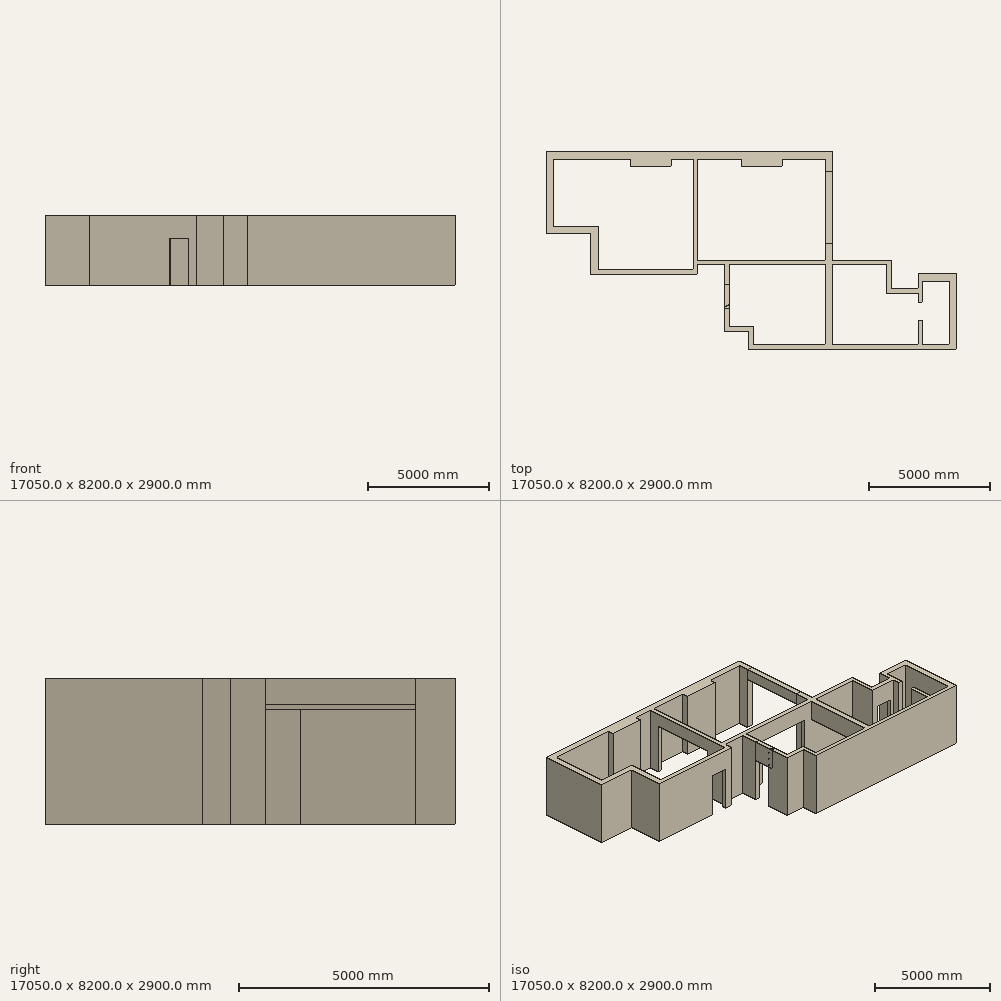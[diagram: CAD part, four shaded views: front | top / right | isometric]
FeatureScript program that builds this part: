
annotation { "Feature Type Name" : "Feature", "Feature Type Description" : "" }
export const myFeature = defineFeature(function(context is Context, id is Id, definition is map)
    precondition{}
    {
        {
            var Q0;
            Q0=qCreatedBy(makeId("Top.planeOp"),FACE);
            var sketch = newSketch(context, id + "F0", { "sketchPlane" : qUnion([Q0])});
            skLineSegment(sketch, "E0", {"start": v(-8264.98, 3800) * mm, "end": v(3635.02, 3800) * mm});
            skLineSegment(sketch, "E1", {"start": v(3635.02, 3800) * mm, "end": v(3635.02, 3000) * mm});
            skLineSegment(sketch, "E2", {"start": v(3635.02, 3000) * mm, "end": v(3335.02, 3000) * mm});
            skLineSegment(sketch, "E3", {"start": v(3335.02, 3000) * mm, "end": v(3335.02, 3500) * mm});
            skLineSegment(sketch, "E4", {"start": v(3335.02, 3500) * mm, "end": v(1535.02, 3500) * mm});
            skLineSegment(sketch, "E5", {"start": v(1535.02, 3500) * mm, "end": v(1535.02, 3200) * mm});
            skLineSegment(sketch, "E6", {"start": v(1535.02, 3200) * mm, "end": v(-164.98, 3200) * mm});
            skLineSegment(sketch, "E7", {"start": v(-164.98, 3200) * mm, "end": v(-164.98, 3500) * mm});
            skLineSegment(sketch, "E8", {"start": v(-164.98, 3500) * mm, "end": v(-1964.98, 3500) * mm});
            skLineSegment(sketch, "E9", {"start": v(-1964.98, 3500) * mm, "end": v(-1964.98, 3000) * mm});
            skLineSegment(sketch, "E10", {"start": v(-1964.98, 3000) * mm, "end": v(-2164.98, 3000) * mm});
            skLineSegment(sketch, "E11", {"start": v(-2164.98, 3000) * mm, "end": v(-2164.98, 3500) * mm});
            skLineSegment(sketch, "E12", {"start": v(-2164.98, 3500) * mm, "end": v(-3064.98, 3500) * mm});
            skLineSegment(sketch, "E13", {"start": v(-3064.98, 3500) * mm, "end": v(-3064.98, 3200) * mm});
            skLineSegment(sketch, "E14", {"start": v(-3064.98, 3200) * mm, "end": v(-4764.98, 3200) * mm});
            skLineSegment(sketch, "E15", {"start": v(-4764.98, 3200) * mm, "end": v(-4764.98, 3500) * mm});
            skLineSegment(sketch, "E16", {"start": v(-4764.98, 3500) * mm, "end": v(-7964.98, 3500) * mm});
            skLineSegment(sketch, "E17", {"start": v(-7964.98, 3500) * mm, "end": v(-7964.98, 700) * mm});
            skLineSegment(sketch, "E18", {"start": v(-7964.98, 700) * mm, "end": v(-6114.98, 700) * mm});
            skLineSegment(sketch, "E19", {"start": v(-6114.98, 700) * mm, "end": v(-6114.98, -1100) * mm});
            skLineSegment(sketch, "E20", {"start": v(-6114.98, -1100) * mm, "end": v(-3114.98, -1100) * mm});
            skLineSegment(sketch, "E21", {"start": v(-2164.98, -1100) * mm, "end": v(-2164.98, 0) * mm});
            skLineSegment(sketch, "E22", {"start": v(-2164.98, 0) * mm, "end": v(-1964.98, 0) * mm});
            skLineSegment(sketch, "E23", {"start": v(-1964.98, 0) * mm, "end": v(-1964.98, -700) * mm});
            skLineSegment(sketch, "E24", {"start": v(-1964.98, -700) * mm, "end": v(335.02, -700) * mm});
            skLineSegment(sketch, "E25", {"start": v(335.02, -700) * mm, "end": v(335.02, -900) * mm});
            skLineSegment(sketch, "E26", {"start": v(335.02, -900) * mm, "end": v(-664.98, -900) * mm});
            skLineSegment(sketch, "E27", {"start": v(-664.98, -900) * mm, "end": v(-664.98, -1700) * mm});
            skLineSegment(sketch, "E28", {"start": v(-664.98, -1700) * mm, "end": v(-864.98, -1700) * mm});
            skLineSegment(sketch, "E29", {"start": v(-864.98, -1700) * mm, "end": v(-864.98, -900) * mm});
            skLineSegment(sketch, "E30", {"start": v(-864.98, -900) * mm, "end": v(-1964.98, -900) * mm});
            skLineSegment(sketch, "E31", {"start": v(-1964.98, -900) * mm, "end": v(-1964.98, -1300) * mm});
            skLineSegment(sketch, "E32", {"start": v(-1964.98, -1300) * mm, "end": v(-2314.98, -1300) * mm});
            skLineSegment(sketch, "E33", {"start": v(-6414.98, -1300) * mm, "end": v(-6414.98, 400) * mm});
            skLineSegment(sketch, "E34", {"start": v(-6414.98, 400) * mm, "end": v(-8264.98, 400) * mm});
            skLineSegment(sketch, "E35", {"start": v(-8264.98, 400) * mm, "end": v(-8264.98, 3800) * mm});
            skLineSegment(sketch, "E36", {"start": v(2935.02, -700) * mm, "end": v(3335.02, -700) * mm});
            skLineSegment(sketch, "E37", {"start": v(3335.02, -700) * mm, "end": v(3335.02, 0) * mm});
            skLineSegment(sketch, "E38", {"start": v(3335.02, 0) * mm, "end": v(3635.02, 0) * mm});
            skLineSegment(sketch, "E39", {"start": v(3635.02, 0) * mm, "end": v(3635.02, -700) * mm});
            skLineSegment(sketch, "E40", {"start": v(3635.02, -700) * mm, "end": v(6085.02, -700) * mm});
            skLineSegment(sketch, "E41", {"start": v(6085.02, -700) * mm, "end": v(6085.02, -1900) * mm});
            skLineSegment(sketch, "E42", {"start": v(3635.02, -4200) * mm, "end": v(3635.02, -3400) * mm});
            skLineSegment(sketch, "E43", {"start": v(3635.02, -3400) * mm, "end": v(3335.02, -3400) * mm});
            skLineSegment(sketch, "E44", {"start": v(3335.02, -3400) * mm, "end": v(3335.02, -4200) * mm});
            skLineSegment(sketch, "E45", {"start": v(3335.02, -4200) * mm, "end": v(335.02, -4200) * mm});
            skLineSegment(sketch, "E46", {"start": v(-3114.98, -1100) * mm, "end": v(-3114.98, -1300) * mm});
            skLineSegment(sketch, "E47", {"start": v(-2314.98, -1300) * mm, "end": v(-2314.98, -1100) * mm});
            skLineSegment(sketch, "E48.trimOffspring", {"start": v(-2314.98, -1100) * mm, "end": v(-2164.98, -1100) * mm});
            skLineSegment(sketch, "E49.trimOffspring", {"start": v(-3114.98, -1300) * mm, "end": v(-6414.98, -1300) * mm});
            skLineSegment(sketch, "E50", {"start": v(2935.02, -700) * mm, "end": v(2935.02, -900) * mm});
            skLineSegment(sketch, "E51", {"start": v(2935.02, -900) * mm, "end": v(5885.02, -900) * mm});
            skLineSegment(sketch, "E52", {"start": v(5885.02, -900) * mm, "end": v(5885.02, -2100) * mm});
            skLineSegment(sketch, "E53", {"start": v(6085.02, -1900) * mm, "end": v(6235.02, -1900) * mm});
            skLineSegment(sketch, "E54", {"start": v(6235.02, -1900) * mm, "end": v(6235.02, -2100) * mm});
            skLineSegment(sketch, "E55", {"start": v(6235.02, -2100) * mm, "end": v(5885.02, -2100) * mm});
            skLineSegment(sketch, "E56", {"start": v(3635.02, -4200) * mm, "end": v(7185.02, -4200) * mm});
            skLineSegment(sketch, "E57", {"start": v(7185.02, -4200) * mm, "end": v(7185.02, -3200) * mm});
            skLineSegment(sketch, "E58", {"start": v(7185.02, -3200) * mm, "end": v(7385.02, -3200) * mm});
            skLineSegment(sketch, "E59", {"start": v(7385.02, -3200) * mm, "end": v(7385.02, -4200) * mm});
            skLineSegment(sketch, "E60", {"start": v(7385.02, -4200) * mm, "end": v(8485.02, -4200) * mm});
            skLineSegment(sketch, "E61", {"start": v(8485.02, -4200) * mm, "end": v(8485.02, -1569) * mm});
            skLineSegment(sketch, "E62", {"start": v(8485.02, -1569) * mm, "end": v(7385.02, -1569) * mm});
            skLineSegment(sketch, "E63", {"start": v(7385.02, -1569) * mm, "end": v(7385.02, -2450) * mm});
            skLineSegment(sketch, "E64", {"start": v(7385.02, -2450) * mm, "end": v(7185.02, -2450) * mm});
            skLineSegment(sketch, "E65", {"start": v(7185.02, -2450) * mm, "end": v(7185.02, -2100) * mm});
            skLineSegment(sketch, "E66", {"start": v(7185.02, -2100) * mm, "end": v(7035.02, -2100) * mm});
            skLineSegment(sketch, "E67", {"start": v(7035.02, -2100) * mm, "end": v(7035.02, -1900) * mm});
            skLineSegment(sketch, "E68", {"start": v(7035.02, -1900) * mm, "end": v(7185.02, -1900) * mm});
            skLineSegment(sketch, "E69", {"start": v(7185.02, -1900) * mm, "end": v(7185.02, -1269) * mm});
            skLineSegment(sketch, "E70", {"start": v(7185.02, -1269) * mm, "end": v(8785.02, -1269) * mm});
            skLineSegment(sketch, "E71", {"start": v(8785.02, -1269) * mm, "end": v(8785.02, -4400) * mm});
            skLineSegment(sketch, "E72", {"start": v(8785.02, -4400) * mm, "end": v(135.02, -4400) * mm});
            skLineSegment(sketch, "E73", {"start": v(135.02, -4400) * mm, "end": v(135.02, -3650) * mm});
            skLineSegment(sketch, "E74", {"start": v(135.02, -3650) * mm, "end": v(-864.98, -3650) * mm});
            skLineSegment(sketch, "E75", {"start": v(-864.98, -3650) * mm, "end": v(-864.98, -2500) * mm});
            skLineSegment(sketch, "E76", {"start": v(-864.98, -2500) * mm, "end": v(-664.98, -2500) * mm});
            skLineSegment(sketch, "E77", {"start": v(-664.98, -2500) * mm, "end": v(-664.98, -3450) * mm});
            skLineSegment(sketch, "E78", {"start": v(-664.98, -3450) * mm, "end": v(335.02, -3450) * mm});
            skLineSegment(sketch, "E79", {"start": v(335.02, -3450) * mm, "end": v(335.02, -4200) * mm});
            skLineSegment(sketch, "E80", {"start": v(-864.98, -1700) * mm, "end": v(-864.98, -2500) * mm, "construction": true});
            skSolve(sketch);
        }
        {
            var Q0;
            Q0=makeQuery(id+"F0.imprint","IMPRINT",FACE,{"disambiguationData":[TD([[makeQuery(id+"F0.imprint","IMPRINT",EDGE,{"derivedFrom":sQuery(id+"F0.wireOp",EDGE,"E0")}),-1.0]])]});
            var Q1;
            Q1=makeQuery(id+"F0.imprint","IMPRINT",FACE,{"disambiguationData":[TD([[makeQuery(id+"F0.imprint","IMPRINT",EDGE,{"derivedFrom":sQuery(id+"F0.wireOp",EDGE,"E21")}),-1.0]])]});
            var Q2;
            Q2=makeQuery(id+"F0.imprint","IMPRINT",FACE,{"disambiguationData":[TD([[makeQuery(id+"F0.imprint","IMPRINT",EDGE,{"derivedFrom":sQuery(id+"F0.wireOp",EDGE,"E36")}),-1.0]])]});
            var Q3;
            Q3=makeQuery(id+"F0.imprint","IMPRINT",FACE,{"disambiguationData":[TD([[makeQuery(id+"F0.imprint","IMPRINT",EDGE,{"derivedFrom":sQuery(id+"F0.wireOp",EDGE,"DD57stPQ-TVIF-p54X-iXXr-weISo5gsyVsJ")}),1.0]])]});
            var Q4;
            Q4=makeQuery(id+"F0.imprint","IMPRINT",FACE,{"disambiguationData":[TD([[makeQuery(id+"F0.imprint","IMPRINT",EDGE,{"derivedFrom":sQuery(id+"F0.wireOp",EDGE,"E42")}),1.0]])]});
            extrude(context, id + "F1", {"entities" : qUnion([Q0, Q1, Q2, Q3, Q4]), "depth" : 2900 * mm, "offsetDistance" : 25 * mm});
        }
        {
            var Q0;
            Q0=makeQuery(id+"F1.opExtrude","SWEPT_FACE",FACE,{"disambiguationData":[OSD([sQuery(id+"F0.wireOp",EDGE,"E2")])]});
            var sketch = newSketch(context, id + "F2", { "sketchPlane" : qUnion([Q0])});
            skLineSegment(sketch, "E81.bottom", {"start": v(3335.02, 2900) * mm, "end": v(3635.02, 2900) * mm});
            skLineSegment(sketch, "E81.top", {"start": v(3335.02, 2400) * mm, "end": v(3635.02, 2400) * mm});
            skLineSegment(sketch, "E81.left", {"start": v(3335.02, 2900) * mm, "end": v(3335.02, 2400) * mm});
            skLineSegment(sketch, "E81.right", {"start": v(3635.02, 2900) * mm, "end": v(3635.02, 2400) * mm});
            skLineSegment(sketch, "E82", {"start": v(3335.02, 0) * mm, "end": v(3335.02, 2400) * mm, "construction": true});
            skSolve(sketch);
        }
        {
            var Q0;
            Q0=makeQuery(id+"F2.imprint","IMPRINT",FACE,{"disambiguationData":[TD([[makeQuery(id+"F2.imprint","IMPRINT",EDGE,{"derivedFrom":sQuery(id+"F2.wireOp",EDGE,"E81.bottom")}),1.0]])]});
            extrude(context, id + "F3", {"entities" : qUnion([Q0]), "depth" : 3000 * mm, "offsetDistance" : 25 * mm});
        }
        {
            var Q0;
            Q0=makeQuery(id+"F1.opExtrude","SWEPT_FACE",FACE,{"disambiguationData":[OSD([sQuery(id+"F0.wireOp",EDGE,"E10")])]});
            var sketch = newSketch(context, id + "F4", { "sketchPlane" : qUnion([Q0])});
            skLineSegment(sketch, "E83.bottom", {"start": v(-2164.98, 2900) * mm, "end": v(-1964.98, 2900) * mm});
            skLineSegment(sketch, "E83.top", {"start": v(-2164.98, 2300) * mm, "end": v(-1964.98, 2300) * mm});
            skLineSegment(sketch, "E83.left", {"start": v(-2164.98, 2900) * mm, "end": v(-2164.98, 2300) * mm});
            skLineSegment(sketch, "E83.right", {"start": v(-1964.98, 2900) * mm, "end": v(-1964.98, 2300) * mm});
            skLineSegment(sketch, "E84", {"start": v(-2164.98, 2300) * mm, "end": v(-2164.98, 0) * mm, "construction": true});
            skSolve(sketch);
        }
        {
            var Q0;
            Q0=makeQuery(id+"F4.imprint","IMPRINT",FACE,{"disambiguationData":[TD([[makeQuery(id+"F4.imprint","IMPRINT",EDGE,{"derivedFrom":sQuery(id+"F4.wireOp",EDGE,"E83.bottom")}),1.0]])]});
            extrude(context, id + "F5", {"entities" : qUnion([Q0]), "operationType" : NewBodyOperationType.ADD, "depth" : 3500 * mm, "offsetDistance" : 25 * mm});
        }
        {
            var Q0;
            Q0=makeQuery(id+"F1.opExtrude","SWEPT_FACE",FACE,{"disambiguationData":[OSD([sQuery(id+"F0.wireOp",EDGE,"E28")])]});
            var sketch = newSketch(context, id + "F6", { "sketchPlane" : qUnion([Q0])});
            skLineSegment(sketch, "E85.bottom", {"start": v(-864.98, 2900) * mm, "end": v(-664.98, 2900) * mm});
            skLineSegment(sketch, "E85.top", {"start": v(-864.98, 1950) * mm, "end": v(-664.98, 1950) * mm});
            skLineSegment(sketch, "E85.left", {"start": v(-864.98, 2900) * mm, "end": v(-864.98, 1950) * mm});
            skLineSegment(sketch, "E85.right", {"start": v(-664.98, 2900) * mm, "end": v(-664.98, 1950) * mm});
            skLineSegment(sketch, "E86", {"start": v(-864.98, 1950) * mm, "end": v(-864.98, 0) * mm, "construction": true});
            skSolve(sketch);
        }
        {
            var Q0;
            Q0=makeQuery(id+"F6.imprint","IMPRINT",FACE,{"disambiguationData":[TD([[makeQuery(id+"F6.imprint","IMPRINT",EDGE,{"derivedFrom":sQuery(id+"F6.wireOp",EDGE,"E85.bottom")}),1.0]])]});
            extrude(context, id + "F7", {"entities" : qUnion([Q0]), "depth" : 1000 * mm, "offsetDistance" : 25 * mm});
        }
        {
            var Q0;
            Q0=makeQuery(id+"F1.opExtrude","SWEPT_FACE",FACE,{"disambiguationData":[OSD([sQuery(id+"F0.wireOp",EDGE,"E46")])]});
            var sketch = newSketch(context, id + "F8", { "sketchPlane" : qUnion([Q0])});
            skLineSegment(sketch, "E87.bottom", {"start": v(-1300, 2900) * mm, "end": v(-1100, 2900) * mm});
            skLineSegment(sketch, "E87.top", {"start": v(-1300, 1950) * mm, "end": v(-1100, 1950) * mm});
            skLineSegment(sketch, "E87.left", {"start": v(-1300, 2900) * mm, "end": v(-1300, 1950) * mm});
            skLineSegment(sketch, "E87.right", {"start": v(-1100, 2900) * mm, "end": v(-1100, 1950) * mm});
            skLineSegment(sketch, "E88", {"start": v(-1300, 1950) * mm, "end": v(-1300, 0) * mm, "construction": true});
            skSolve(sketch);
        }
        {
            var Q0;
            Q0=makeQuery(id+"F8.imprint","IMPRINT",FACE,{"disambiguationData":[TD([[makeQuery(id+"F8.imprint","IMPRINT",EDGE,{"derivedFrom":sQuery(id+"F8.wireOp",EDGE,"E87.bottom")}),1.0]])]});
            extrude(context, id + "F9", {"entities" : qUnion([Q0]), "operationType" : NewBodyOperationType.ADD, "depth" : 1000 * mm, "offsetDistance" : 25 * mm});
        }
        {
            var Q0;
            Q0=makeQuery(id+"F1.opExtrude","SWEPT_FACE",FACE,{"disambiguationData":[OSD([sQuery(id+"F0.wireOp",EDGE,"E25")])]});
            var sketch = newSketch(context, id + "F10", { "sketchPlane" : qUnion([Q0])});
            skLineSegment(sketch, "E89.bottom", {"start": v(-900, 2900) * mm, "end": v(-700, 2900) * mm});
            skLineSegment(sketch, "E89.top", {"start": v(-900, 2100) * mm, "end": v(-700, 2100) * mm});
            skLineSegment(sketch, "E89.left", {"start": v(-900, 2900) * mm, "end": v(-900, 2100) * mm});
            skLineSegment(sketch, "E89.right", {"start": v(-700, 2900) * mm, "end": v(-700, 2100) * mm});
            skLineSegment(sketch, "E90", {"start": v(-900, 2100) * mm, "end": v(-900, 0) * mm, "construction": true});
            skSolve(sketch);
        }
        {
            var Q0;
            Q0=makeQuery(id+"F10.imprint","IMPRINT",FACE,{"disambiguationData":[TD([[makeQuery(id+"F10.imprint","IMPRINT",EDGE,{"derivedFrom":sQuery(id+"F10.wireOp",EDGE,"E89.bottom")}),1.0]])]});
            extrude(context, id + "F11", {"entities" : qUnion([Q0]), "operationType" : NewBodyOperationType.ADD, "depth" : 3000 * mm, "offsetDistance" : 25 * mm});
        }
        {
            var Q0;
            Q0=makeQuery(id+"F1.opExtrude","SWEPT_FACE",FACE,{"disambiguationData":[OSD([sQuery(id+"F0.wireOp",EDGE,"E43")])]});
            var sketch = newSketch(context, id + "F12", { "sketchPlane" : qUnion([Q0])});
            skLineSegment(sketch, "E91.bottom", {"start": v(-3635.02, 2900) * mm, "end": v(-3335.02, 2900) * mm});
            skLineSegment(sketch, "E91.top", {"start": v(-3635.02, 2000) * mm, "end": v(-3335.02, 2000) * mm});
            skLineSegment(sketch, "E91.left", {"start": v(-3635.02, 2900) * mm, "end": v(-3635.02, 2000) * mm});
            skLineSegment(sketch, "E91.right", {"start": v(-3335.02, 2900) * mm, "end": v(-3335.02, 2000) * mm});
            skLineSegment(sketch, "E92", {"start": v(-3635.02, 2000) * mm, "end": v(-3635.02, 0) * mm, "construction": true});
            skSolve(sketch);
        }
        {
            var Q0;
            Q0=makeQuery(id+"F12.imprint","IMPRINT",FACE,{"disambiguationData":[TD([[makeQuery(id+"F12.imprint","IMPRINT",EDGE,{"derivedFrom":sQuery(id+"F12.wireOp",EDGE,"E91.bottom")}),-1.0]])]});
            extrude(context, id + "F13", {"entities" : qUnion([Q0]), "operationType" : NewBodyOperationType.ADD, "depth" : 2580 * mm, "offsetDistance" : 25 * mm});
        }
        {
            var Q0;
            Q0=makeQuery(id+"F1.opExtrude","SWEPT_FACE",FACE,{"disambiguationData":[OSD([sQuery(id+"F0.wireOp",EDGE,"E54")])]});
            var sketch = newSketch(context, id + "F14", { "sketchPlane" : qUnion([Q0])});
            skLineSegment(sketch, "E93.bottom", {"start": v(-2100, 2900) * mm, "end": v(-1900, 2900) * mm});
            skLineSegment(sketch, "E93.top", {"start": v(-2100, 1950) * mm, "end": v(-1900, 1950) * mm});
            skLineSegment(sketch, "E93.left", {"start": v(-2100, 2900) * mm, "end": v(-2100, 1950) * mm});
            skLineSegment(sketch, "E93.right", {"start": v(-1900, 2900) * mm, "end": v(-1900, 1950) * mm});
            skLineSegment(sketch, "E94", {"start": v(-2100, 1950) * mm, "end": v(-2100, 0) * mm, "construction": true});
            skSolve(sketch);
        }
        {
            var Q0;
            Q0=makeQuery(id+"F14.imprint","IMPRINT",FACE,{"disambiguationData":[TD([[makeQuery(id+"F14.imprint","IMPRINT",EDGE,{"derivedFrom":sQuery(id+"F14.wireOp",EDGE,"E93.bottom")}),1.0]])]});
            extrude(context, id + "F15", {"entities" : qUnion([Q0]), "operationType" : NewBodyOperationType.ADD, "depth" : 830 * mm, "offsetDistance" : 25 * mm});
        }
    });
